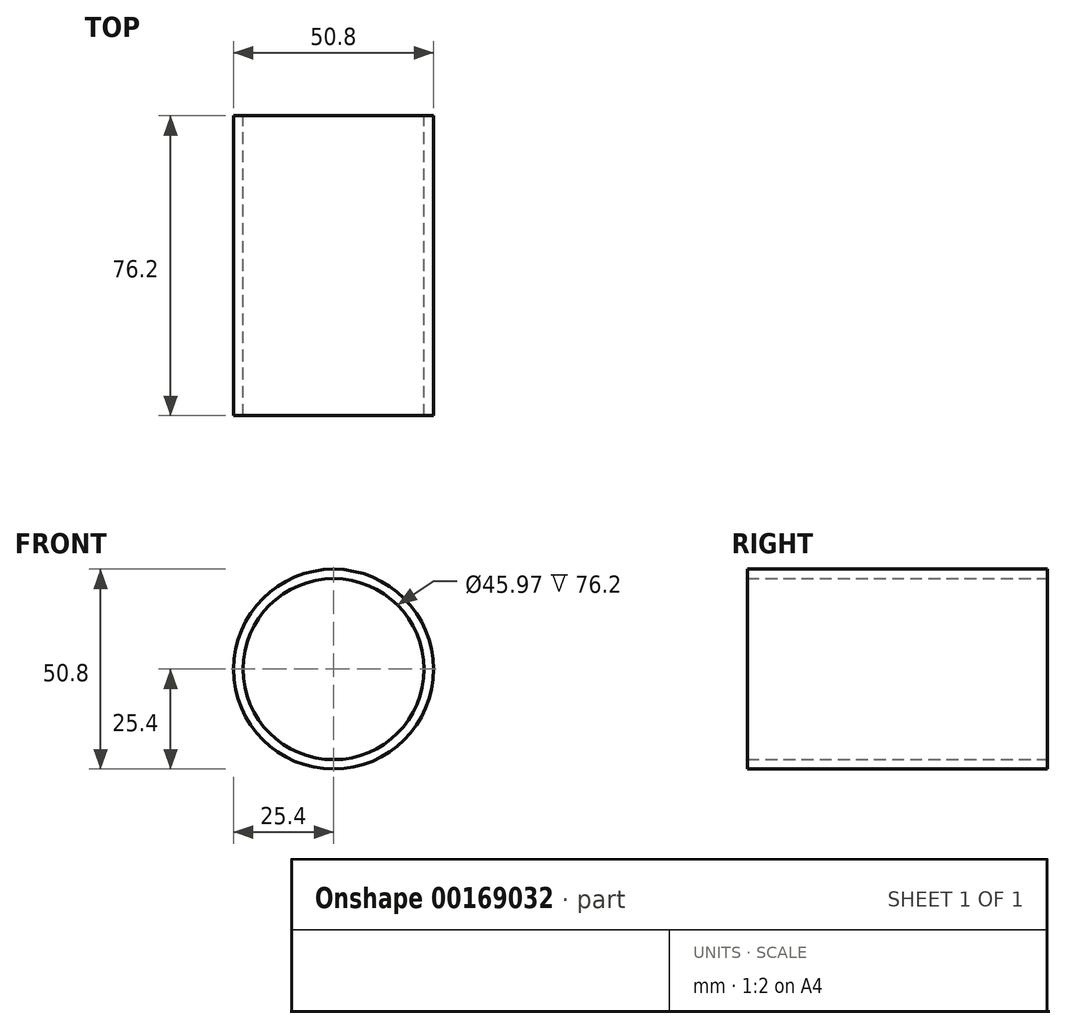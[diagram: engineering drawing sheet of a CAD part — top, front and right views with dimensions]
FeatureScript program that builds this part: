
annotation { "Feature Type Name" : "Feature", "Feature Type Description" : "" }
export const myFeature = defineFeature(function(context is Context, id is Id, definition is map)
    precondition{}
    {
        {
            var Q0;
            Q0=qCreatedBy(makeId("Front.planeOp"),FACE);
            var sketch = newSketch(context, id + "F0", { "sketchPlane" : qUnion([Q0])});
            skCircle(sketch, "E0", {"center": v(0, 0) * mm, "radius": 22.99 * mm});
            skCircle(sketch, "E1", {"center": v(0, 0) * mm, "radius": 25.4 * mm});
            skSolve(sketch);
        }
        {
            var Q0;
            Q0=makeQuery(id+"F0.imprint","IMPRINT",FACE,{"disambiguationData":[TD([[makeQuery(id+"F0.imprint","IMPRINT",EDGE,{"derivedFrom":sQuery(id+"F0.wireOp",EDGE,"E0")}),-1.0]])]});
            extrude(context, id + "F1", {"entities" : qUnion([Q0]), "depth" : 76.2 * mm});
        }
    });
